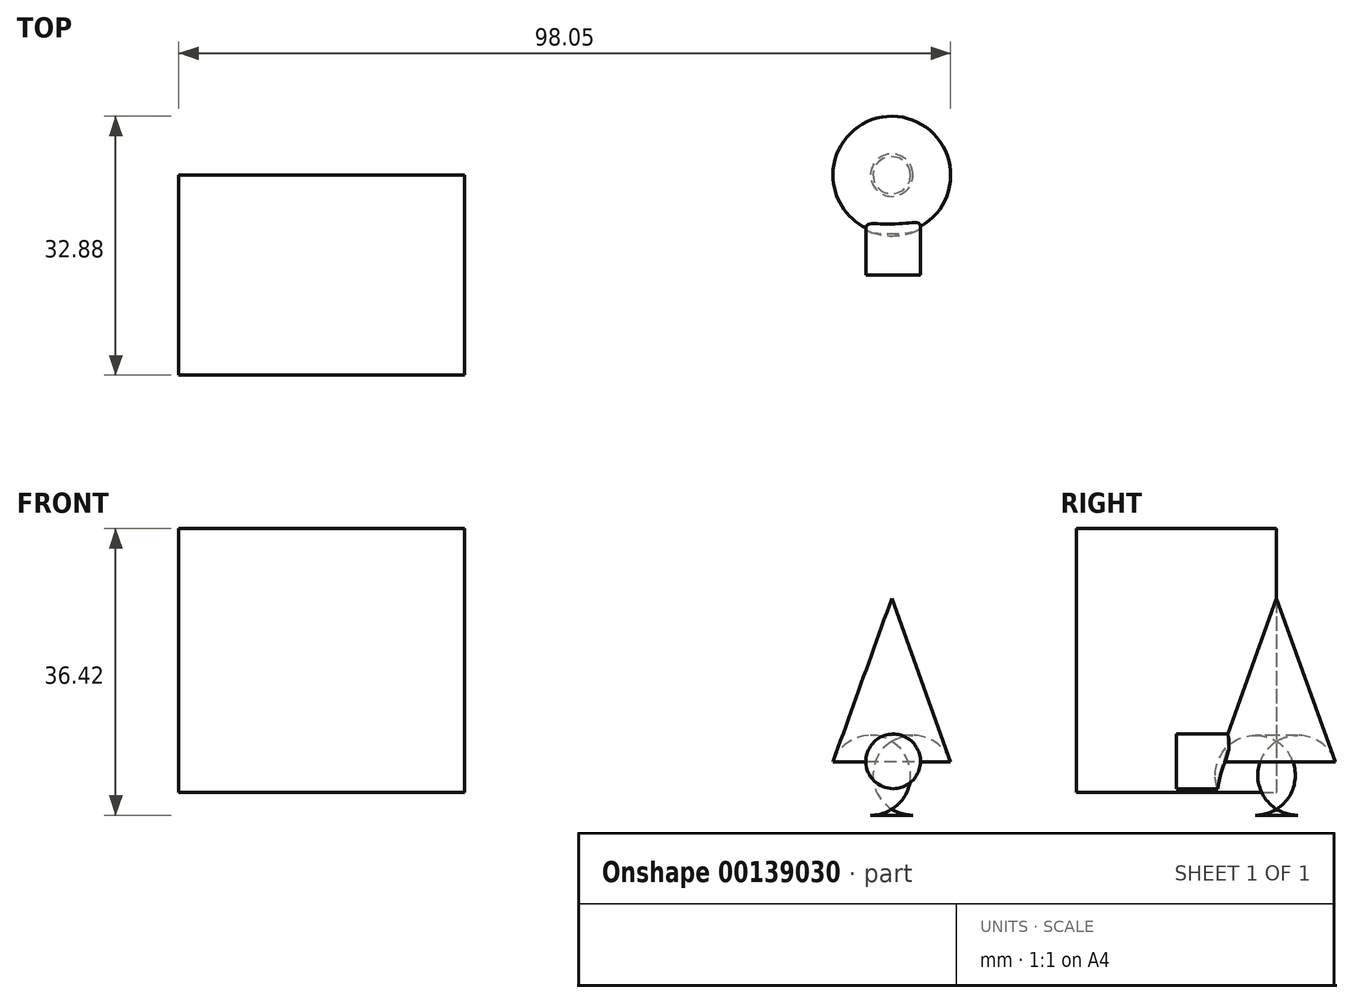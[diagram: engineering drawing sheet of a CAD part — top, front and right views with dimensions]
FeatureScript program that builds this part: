
annotation { "Feature Type Name" : "Feature", "Feature Type Description" : "" }
export const myFeature = defineFeature(function(context is Context, id is Id, definition is map)
    precondition{}
    {
        {
            var Q0;
            Q0=qCreatedBy(makeId("Front.planeOp"),FACE);
            var sketch = newSketch(context, id + "F0", { "sketchPlane" : qUnion([Q0])});
            skLineSegment(sketch, "E0", {"start": v(34.23, 9.33) * mm, "end": v(34.23, 36.88) * mm});
            skLineSegment(sketch, "E1", {"start": v(34.23, 9.33) * mm, "end": v(24.3, 9.33) * mm});
            skLineSegment(sketch, "E2", {"start": v(24.3, 9.33) * mm, "end": v(34.23, 36.88) * mm});
            skSolve(sketch);
        }
        {
            var Q0;
            Q0=makeQuery(id+"F0.imprint","IMPRINT",FACE,{"disambiguationData":[TD([[makeQuery(id+"F0.imprint","IMPRINT",EDGE,{"derivedFrom":sQuery(id+"F0.wireOp",EDGE,"E0")}),1.0]])]});
            var Q1;
            Q1=sQuery(id+"F0.wireOp",EDGE,"E0");
            revolve(context, id + "F1", {"entities" : qUnion([Q0]), "axis" : qUnion([Q1]), "revolveType" : RevolveType.FULL});
        }
        {
            var Q0;
            Q0=qCreatedBy(makeId("Front.planeOp"),FACE);
            var sketch = newSketch(context, id + "F2", { "sketchPlane" : qUnion([Q0])});
            skLineSegment(sketch, "E3.bottom", {"start": v(-56.35, 45.75) * mm, "end": v(-20.05, 45.75) * mm});
            skLineSegment(sketch, "E3.top", {"start": v(-56.35, 12.22) * mm, "end": v(-20.05, 12.22) * mm});
            skLineSegment(sketch, "E3.left", {"start": v(-56.35, 45.75) * mm, "end": v(-56.35, 12.22) * mm});
            skLineSegment(sketch, "E3.right", {"start": v(-20.05, 45.75) * mm, "end": v(-20.05, 12.22) * mm});
            skSolve(sketch);
        }
        {
            var Q0;
            Q0=makeQuery(id+"F2.imprint","IMPRINT",FACE,{"disambiguationData":[TD([[makeQuery(id+"F2.imprint","IMPRINT",EDGE,{"derivedFrom":sQuery(id+"F2.wireOp",EDGE,"E3.bottom")}),-1.0]])]});
            extrude(context, id + "F3", {"entities" : qUnion([Q0]), "depth" : 25.4 * mm});
        }
        {
            var Q0;
            Q0=makeQuery(id+"F1.opRevolve","SWEPT_EDGE",EDGE,{"disambiguationData":[OSD([sQuery(id+"F0.wireOp",EDGE,"E1"),sQuery(id+"F0.wireOp",EDGE,"E2")])]});
            fillet(context, id + "F4", {"entities" : qUnion([Q0]), "radius" : 5.08 * mm, "tangentPropagation" : true, "allowEdgeOverflow" : false});
        }
        {
            var Q0;
            Q0=qCreatedBy(makeId("Front.planeOp"),FACE);
            var sketch = newSketch(context, id + "F5", { "sketchPlane" : qUnion([Q0])});
            skCircle(sketch, "E4", {"center": v(34.4, 16.17) * mm, "radius": 3.47 * mm});
            skSolve(sketch);
        }
        {
            var Q0;
            Q0 = qSketchRegion(id + "F5", true);
            extrude(context, id + "F6", {"entities" : qUnion([Q0]), "operationType" : NewBodyOperationType.ADD, "depth" : 12.7 * mm});
        }
    });
